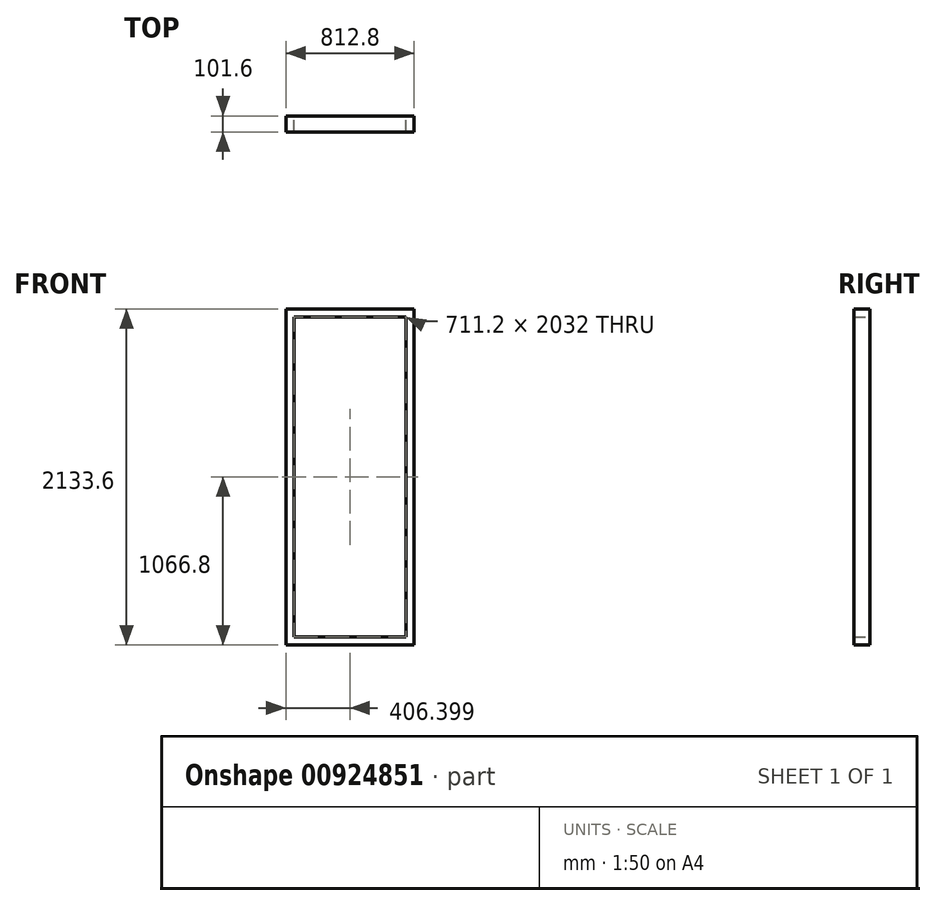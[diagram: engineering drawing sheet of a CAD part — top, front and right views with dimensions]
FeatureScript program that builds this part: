
annotation { "Feature Type Name" : "Feature", "Feature Type Description" : "" }
export const myFeature = defineFeature(function(context is Context, id is Id, definition is map)
    precondition{}
    {
        {
            var Q0;
            Q0=qCreatedBy(makeId("Front.planeOp"),FACE);
            var sketch = newSketch(context, id + "F0", { "sketchPlane" : qUnion([Q0])});
            skLineSegment(sketch, "E0.bottom", {"start": v(-798.21, 1988.5) * mm, "end": v(-87.01, 1988.5) * mm});
            skLineSegment(sketch, "E0.top", {"start": v(-798.21, -43.5) * mm, "end": v(-87.01, -43.5) * mm});
            skLineSegment(sketch, "E0.left", {"start": v(-798.21, 1988.5) * mm, "end": v(-798.21, -43.5) * mm});
            skLineSegment(sketch, "E0.right", {"start": v(-87.01, 1988.5) * mm, "end": v(-87.01, -43.5) * mm});
            skLineSegment(sketch, "E1.0", {"start": v(-849.01, 2039.3) * mm, "end": v(-36.21, 2039.3) * mm});
            skLineSegment(sketch, "E1.1", {"start": v(-849.01, 2039.3) * mm, "end": v(-849.01, -94.3) * mm});
            skLineSegment(sketch, "E1.2", {"start": v(-849.01, -94.3) * mm, "end": v(-36.21, -94.3) * mm});
            skLineSegment(sketch, "E1.3", {"start": v(-36.21, 2039.3) * mm, "end": v(-36.21, -94.3) * mm});
            skSolve(sketch);
        }
        {
            var Q0;
            Q0=makeQuery(id+"F0.imprint","IMPRINT",FACE,{"disambiguationData":[TD([[makeQuery(id+"F0.imprint","IMPRINT",EDGE,{"derivedFrom":sQuery(id+"F0.wireOp",EDGE,"E0.bottom")}),1.0]])]});
            extrude(context, id + "F1", {"entities" : qUnion([Q0]), "depth" : 101.6 * mm, "offsetDistance" : 25.4 * mm});
        }
    });
